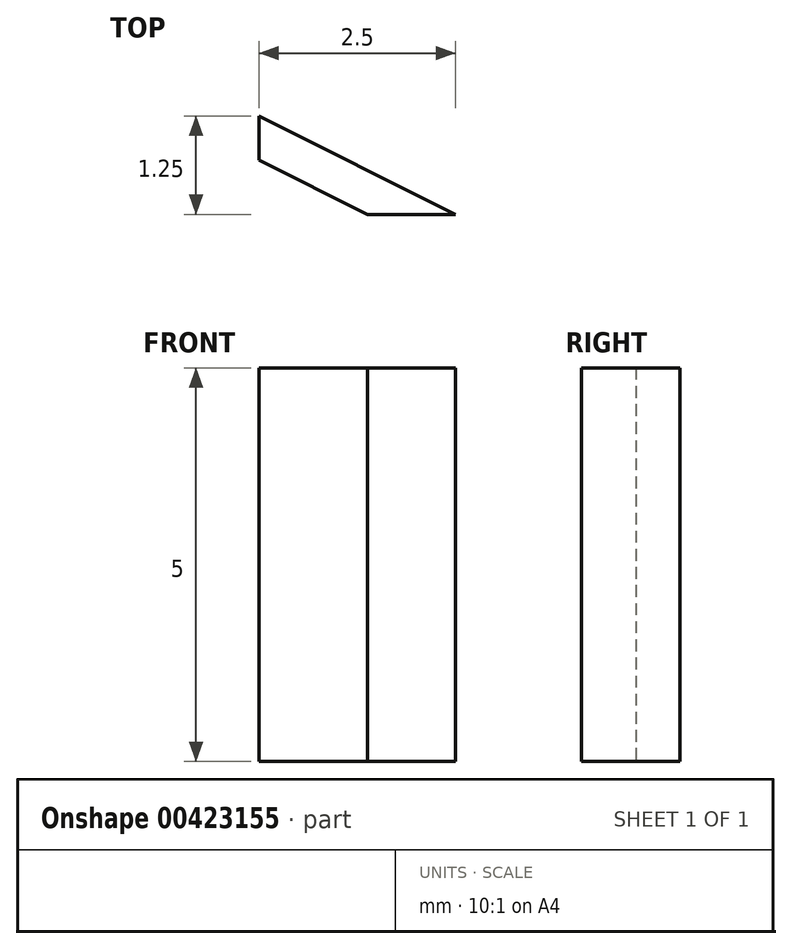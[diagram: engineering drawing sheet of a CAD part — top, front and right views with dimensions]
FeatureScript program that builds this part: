
annotation { "Feature Type Name" : "Feature", "Feature Type Description" : "" }
export const myFeature = defineFeature(function(context is Context, id is Id, definition is map)
    precondition{}
    {
        {
            assignVariable(context, id + "F0", {"variableType" : VariableType.LENGTH, "name" : "spring_diameter", "lengthValue" : 5 * mm});
        }
        {
            var Q0;
            Q0=qCreatedBy(makeId("Top.planeOp"),FACE);
            var sketch = newSketch(context, id + "F1", { "sketchPlane" : qUnion([Q0])});
            skLineSegment(sketch, "E0", {"start": v(0, 0.7) * mm, "end": v(1.38, 0) * mm});
            skLineSegment(sketch, "E1", {"start": v(0, 0.7) * mm, "end": v(0, 1.25) * mm});
            skLineSegment(sketch, "E2", {"start": v(0, 1.25) * mm, "end": v(2.5, 0) * mm});
            skLineSegment(sketch, "E3", {"start": v(2.5, 0) * mm, "end": v(1.38, 0) * mm});
            skSolve(sketch);
        }
        {
            var Q0;
            Q0=makeQuery(id+"FHgEsbuxiMPabYW_0.1.FUDDMkIEQ4LDAuT_0.1.F1.imprint","IMPRINT",FACE,{"disambiguationData":[TD([[makeQuery(id+"FHgEsbuxiMPabYW_0.1.FUDDMkIEQ4LDAuT_0.1.F1.imprint","IMPRINT",EDGE,{"derivedFrom":sQuery(id+"FHgEsbuxiMPabYW_0.1.FUDDMkIEQ4LDAuT_0.1.F1.wireOp",EDGE,"E0")}),1.0]])]});
            var Q1;
            Q1=makeQuery(id+"FUDDMkIEQ4LDAuT_0.1.F1.imprint","IMPRINT",FACE,{"disambiguationData":[TD([[makeQuery(id+"FUDDMkIEQ4LDAuT_0.1.F1.imprint","IMPRINT",EDGE,{"derivedFrom":sQuery(id+"FUDDMkIEQ4LDAuT_0.1.F1.wireOp",EDGE,"E0")}),1.0]])]});
            var Q2;
            Q2=makeQuery(id+"F1.imprint","IMPRINT",FACE,{"disambiguationData":[TD([[makeQuery(id+"F1.imprint","IMPRINT",EDGE,{"derivedFrom":sQuery(id+"F1.wireOp",EDGE,"E0")}),1.0]])]});
            var Q3;
            Q3=makeQuery(id+"FHgEsbuxiMPabYW_0.1.F1.imprint","IMPRINT",FACE,{"disambiguationData":[TD([[makeQuery(id+"FHgEsbuxiMPabYW_0.1.F1.imprint","IMPRINT",EDGE,{"derivedFrom":sQuery(id+"FHgEsbuxiMPabYW_0.1.F1.wireOp",EDGE,"E0")}),1.0]])]});
            extrude(context, id + "F2", {"entities" : qUnion([Q0, Q1, Q2, Q3]), "depth" : getVariable(context, 'spring_diameter'), "offsetDistance" : 25 * mm});
        }
    });
